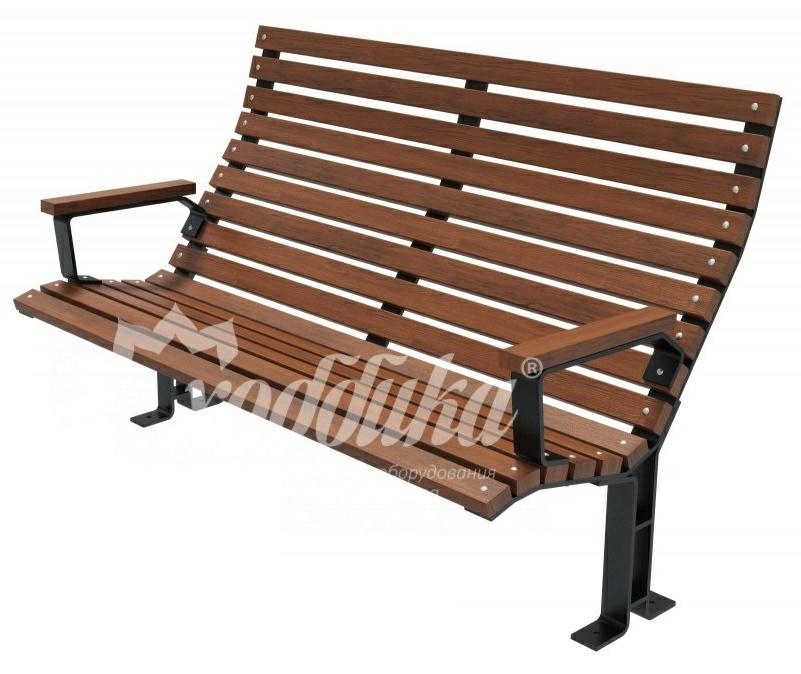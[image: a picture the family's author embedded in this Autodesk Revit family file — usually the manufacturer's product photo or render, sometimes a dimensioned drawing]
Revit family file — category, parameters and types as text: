
# Revit family: Скамейка стальная «Лакус» Арт 13230
name_source: partatom
category: Антураж
revit_build: Autodesk Revit 2018 (Build: 20180423_1000(x64)
units: mm (PartAtom-declared; Revit-internal decimal feet)

## family parameters
Всегда вертикально = Да
Источник визуального образа = Геометрия семейства
На основе рабочей плоскости = Нет
Общий = Нет
При загрузке вырезать с полостями = Нет
Точка расчета площади = Нет

## types (6) — shared parameters
URL = https://hobbyka.ru
Артикул товара = Арт. 13230
Высота = 1000 мм
Группа модели = Садовые скамейки
Изготовитель = ООО «Хоббика»
Материал изделия = Сталь, дерево
Цвет лавки = Дерево
Цвет опоры = Сталь
Ширина = 810 мм

## per-type parameters (varying)
| type | Версия 1,5 м | Версия 1,5 м с опорой | Версия 1,8 м | Версия 1,8 м с опорой | Версия 2,0 м | Версия 2,0 м с опорой | Длина | Изображение типоразмера | Описание | Опора для ног | Средняя опора | Средняя опора для ног |
| Версия 1,5 м | Да | Нет | Нет | Нет | Нет | Нет | 1500 мм | Скамейка стальная «Лакус» Арт 13230 без опоры.jpg | Скамейка стальная «Лакус». Верси 1,5 м | Нет | Нет | Нет |
| Версия 1,5 м с опорой | Нет | Да | Нет | Нет | Нет | Нет | 1500 мм | Скамейка стальная «Лакус» Арт 13230 с опорой.jpg | Скамейка стальная «Лакус». Версия 1,5 м с опорой для ног | Да | Нет | Нет |
| Версия 1,8 м | Нет | Нет | Да | Нет | Нет | Нет | 1800 мм | Скамейка стальная «Лакус» Арт 13230 без опоры.jpg | Скамейка стальная «Лакус». Верси 1,8 м | Нет | Нет | Нет |
| Версия 1,8 с опорой | Нет | Нет | Нет | Да | Нет | Нет | 1800 мм | Скамейка стальная «Лакус» Арт 13230 с опорой.jpg | Скамейка стальная «Лакус». Версия 1,8 м с опорой для ног | Да | Нет | Нет |
| Версия 2,0 м | Нет | Нет | Нет | Нет | Да | Нет | 2000 мм | Скамейка стальная «Лакус» Арт 13230 без опоры.jpg | Скамейка стальная «Лакус». Верси 2,0 м | Нет | Да | Нет |
| Версия 2,0 м с опорой | Нет | Нет | Нет | Нет | Нет | Да | 2000 мм | Скамейка стальная «Лакус» Арт 13230 с опорой.jpg | Скамейка стальная «Лакус». Версия 2,0 м с опорой для ног | Да | Да | Да |
